FCSTD DOCUMENT  (FreeCAD 0.21R33771 (Git))
Label: Assembly
License: All rights reserved
LicenseURL: http://en.wikipedia.org/wiki/All_rights_reserved
objects: App::Link×43, Part::Feature×8, App::Part×8, PartDesign::CoordinateSystem×7, App::DocumentObjectGroup×3, App::FeaturePython×1
note: 15 computed .brp shape members not serialized (recipe doc carries the construction recipe); baked Part::Feature solids carry a one-line shape summary decoded from their .brp
EXTERNAL_REF file=Azi Plate.FCStd obj=Local_CS
EXTERNAL_REF file=Azi Plate.FCStd obj=Body
EXTERNAL_REF file=Alt Plate Center.FCStd obj=Local_CS002
EXTERNAL_REF file=Alt Plate Center.FCStd obj=Body
EXTERNAL_REF file=Alt Plate.FCStd obj=Local_CS
EXTERNAL_REF file=Alt Plate Center.FCStd obj=Local_CS
EXTERNAL_REF file=Alt Plate.FCStd obj=Body
EXTERNAL_REF file=Alt Plate.FCStd obj=Local_CS001
EXTERNAL_REF file=Alt Plate Center.FCStd obj=Local_CS001
EXTERNAL_REF file=Alt Plate Center.FCStd obj=Local_CS004
EXTERNAL_REF file=Pin.FCStd obj=Local_CS
EXTERNAL_REF file=Pin.FCStd obj=Body
EXTERNAL_REF file=Alt Plate.FCStd obj=Local_CS002
EXTERNAL_REF file=Couple Plate.FCStd obj=Local_CS004
EXTERNAL_REF file=Couple Plate.FCStd obj=Body
EXTERNAL_REF file=Couple Plate.FCStd obj=Local_CS
EXTERNAL_REF file=Disk.FCStd obj=Local_CS
EXTERNAL_REF file=Disk.FCStd obj=Body002
EXTERNAL_REF file=Spacer.FCStd obj=Local_CS001
EXTERNAL_REF file=Spacer.FCStd obj=Body
EXTERNAL_REF file=Spacer.FCStd obj=Local_CS
EXTERNAL_REF file=Lower Bearing Block.FCStd obj=Local_CS
EXTERNAL_REF file=Lower Bearing Block.FCStd obj=Body
EXTERNAL_REF file=Lower Bearing Block.FCStd obj=Local_CS001
EXTERNAL_REF file=Connector Plate.FCStd obj=Local_CS001
EXTERNAL_REF file=Lower Bearing Block.FCStd obj=Local_CS003
EXTERNAL_REF file=Connector Plate.FCStd obj=Body
EXTERNAL_REF file=Connector Plate.FCStd obj=Local_CS
EXTERNAL_REF file=Upper Bearing Block.FCStd obj=Local_CS
EXTERNAL_REF file=Upper Bearing Block.FCStd obj=Body
EXTERNAL_REF file=Hand Nut.FCStd obj=Local_CS
EXTERNAL_REF file=Hand Nut.FCStd obj=Body
EXTERNAL_REF file=Upper Bearing Block.FCStd obj=Local_CS001
EXTERNAL_REF file=Upper Plate.FCStd obj=Local_CS
EXTERNAL_REF file=Upper Plate.FCStd obj=Body004
EXTERNAL_REF file=Upper Plate.FCStd obj=Local_CS005
EXTERNAL_REF file=Flange Bearing.FCStd obj=Local_CS
EXTERNAL_REF file=Upper Plate.FCStd obj=Local_CS003
EXTERNAL_REF file=Flange Bearing.FCStd obj=Body003
EXTERNAL_REF file=Upper Plate.FCStd obj=Local_CS004
EXTERNAL_REF file=Upper Plate.FCStd obj=Local_CS001
EXTERNAL_REF file=Upper Plate.FCStd obj=Local_CS002
EXTERNAL_REF file=Motor Plate.FCStd obj=Local_CS
EXTERNAL_REF file=Upper Plate.FCStd obj=Local_CS007
EXTERNAL_REF file=Motor Plate.FCStd obj=Body
EXTERNAL_REF file=Upper Plate.FCStd obj=Local_CS006
EXTERNAL_REF file=Flange Bearing.FCStd obj=Local_CS001
EXTERNAL_REF file=Motor Plate.FCStd obj=Local_CS001
EXTERNAL_REF file=Holder.FCStd obj=Local_CS
EXTERNAL_REF file=Holder.FCStd obj=Body
EXTERNAL_REF file=Holder.FCStd obj=Local_CS001
EXTERNAL_REF file=Holder Pad.FCStd obj=Local_CS
EXTERNAL_REF file=Holder Pad.FCStd obj=Body
EXTERNAL_REF file=Channel.FCStd obj=DatumPoint
EXTERNAL_REF file=Holder Pad.FCStd obj=Local_CS001
EXTERNAL_REF file=Channel.FCStd obj=Body
EXTERNAL_REF file=Anchor Plate.FCStd obj=Body
EXTERNAL_REF file=Anchor Plate.FCStd obj=Local_CS001
EXTERNAL_REF file=Anchor Plate.FCStd obj=Local_CS002
EXTERNAL_REF file=Alt Plate Center.FCStd obj=Local_CS003

FEATURE [PartDesign::CoordinateSystem] LCS_Origin
  AttacherType = Attacher::AttachEngine3D
  MapMode = 2
  Support = -> [X_Axis]
FEATURE [App::DocumentObjectGroup] Constraints
FEATURE [App::FeaturePython] Variables  # WARN: FeaturePython — macro-defined, semantics opaque (R4)
  Type = App::PropertyContainer
  alt = -90
  azi = -10
  dec = 0
  ra = 180
FEATURE [App::DocumentObjectGroup] Configurations
FEATURE [App::Link] Azi_Plate  label="Azi Plate"
  AttachedBy = #Local_CS
  AttachedTo = Alt_Plate_Center#Local_CS001
  AttachmentOffset = pos=(0,0,0) rot=(1,0,0;3.14159rad)
  LinkPlacement = pos=(5e-16,3e-16,-6.35) rot=(0,0,-1;1.5708rad)
  LinkedObject = -> <external Azi Plate.FCStd>#Body
  Placement = pos=(5e-16,3e-16,-6.35) rot=(0,0,-1;1.5708rad)
  SolverId = Asm4EE
  expr: Placement = LCS_Origin.Placement * AttachmentOffset * Azi_Plate#Local_CS.Placement ^ -1
FEATURE [App::Link] Alt_Plate_Center  label="Alt Plate Center"
  AttachedBy = #Local_CS002
  AttachedTo = Azi_Plate#Local_CS
  LinkPlacement = pos=(2.5e-15,6.5e-15,16) rot=(0,0,1;0rad)
  LinkedObject = -> <external Alt Plate Center.FCStd>#Body
  Placement = pos=(2.5e-15,6.5e-15,16) rot=(0,0,1;0rad)
  SolverId = Asm4EE
  expr: Placement = Azi_Plate.Placement * Azi_Plate#Local_CS.Placement * AttachmentOffset * Alt_Plate_Center#Local_CS002.Placement ^ -1
FEATURE [App::Link] Alt_Plate  label="Alt Plate"
  AttachedBy = #Local_CS001
  AttachedTo = Alt_Plate_Center#Local_CS001
  AttachmentOffset = pos=(0,0,1.6) rot=(0,0,1;-1.5708rad)
  LinkPlacement = pos=(4e-15,-17.475,32.0697) rot=(0,-1,0;4.71239rad)
  LinkedObject = -> <external Alt Plate.FCStd>#Body
  Placement = pos=(4e-15,-17.475,32.0697) rot=(0,-1,0;4.71239rad)
  SolverId = Asm4EE
  expr: .AttachmentOffset.Rotation.Angle = Variables.alt
  expr: Placement = Alt_Plate_Center.Placement * Alt_Plate_Center#Local_CS.Placement * AttachmentOffset * Alt_Plate#Local_CS.Placement ^ -1
FEATURE [App::Link] Alt_Plate001  label="Alt Plate001"
  AttachedBy = #Local_CS001
  AttachedTo = Alt_Plate_Center#Local_CS
  AttachmentOffset = pos=(0,0,-1.6) rot=(0,0,1;-1.5708rad)
  LinkPlacement = pos=(4.9e-15,17.475,32.0697) rot=(0,-1,0;4.71239rad)
  LinkedObject = -> <external Alt Plate.FCStd>#Body
  Placement = pos=(4.9e-15,17.475,32.0697) rot=(0,-1,0;4.71239rad)
  SolverId = Asm4EE
  expr: .AttachmentOffset.Rotation.Angle = Variables.alt
  expr: Placement = Alt_Plate_Center.Placement * Alt_Plate_Center#Local_CS001.Placement * AttachmentOffset * Alt_Plate#Local_CS001.Placement ^ -1
FEATURE [App::Link] Pin
  AttachedBy = #Local_CS
  AttachedTo = Alt_Plate_Center#Local_CS004
  AttachmentOffset = pos=(0,0,0) rot=(0.707107,0.707107,0;3.14159rad)
  LinkPlacement = pos=(-0.000223577,-8.77746e-06,16) rot=(0,1,-2e-06;3.14159rad)
  LinkedObject = -> <external Pin.FCStd>#Body
  Placement = pos=(-0.000223577,-8.77746e-06,16) rot=(0,1,-2e-06;3.14159rad)
  SolverId = Asm4EE
  expr: Placement = Alt_Plate_Center.Placement * Alt_Plate_Center#Local_CS004.Placement * AttachmentOffset * Pin#Local_CS.Placement ^ -1
FEATURE [App::Link] Couple_Plate  label="Couple Plate"
  AttachedBy = #Local_CS004
  AttachedTo = Alt_Plate#Local_CS002
  AttachmentOffset = pos=(0,0,0) rot=(0.707107,-0.707107,0;3.14159rad)
  LinkPlacement = pos=(50,-3.18,32.0697) rot=(-0.57735,0.57735,0.57735;4.18879rad)
  LinkedObject = -> <external Couple Plate.FCStd>#Body
  Placement = pos=(50,-3.18,32.0697) rot=(-0.57735,0.57735,0.57735;4.18879rad)
  SolverId = Asm4EE
  expr: Placement = Alt_Plate.Placement * Alt_Plate#Local_CS002.Placement * AttachmentOffset * Couple_Plate#Local_CS004.Placement ^ -1
FEATURE [App::Link] Disk
  AttachedBy = #Local_CS
  AttachedTo = Couple_Plate#Local_CS
  AttachmentOffset = pos=(0,0,0) rot=(1,0,0;3.14159rad)
  LinkPlacement = pos=(59.525,-3.18,32.0697) rot=(0.57735,-0.57735,-0.57735;2.0944rad)
  LinkedObject = -> <external Disk.FCStd>#Body002
  Placement = pos=(59.525,-3.18,32.0697) rot=(0.57735,-0.57735,-0.57735;2.0944rad)
  SolverId = Asm4EE
  expr: Placement = Couple_Plate.Placement * Couple_Plate#Local_CS.Placement * AttachmentOffset * Disk#Local_CS.Placement ^ -1
FEATURE [App::Link] Spacer
  AttachedBy = #Local_CS001
  AttachedTo = Disk#Local_CS
  AttachmentOffset = pos=(0,0,-10) rot=(1,0,0;3.14159rad)
  LinkPlacement = pos=(60,-3.18,32.0697) rot=(0.57735,0.57735,0.57735;2.0944rad)
  LinkedObject = -> <external Spacer.FCStd>#Body
  Placement = pos=(60,-3.18,32.0697) rot=(0.57735,0.57735,0.57735;2.0944rad)
  SolverId = Asm4EE
  expr: Placement = Disk.Placement * Disk#Local_CS.Placement * AttachmentOffset * Spacer#Local_CS001.Placement ^ -1
FEATURE [PartDesign::CoordinateSystem] LCS_0
  AttacherType = Attacher::AttachEngine3D
  MapMode = 2
  Support = -> [X_Axis001]
FEATURE [Part::Feature] Part__Feature  label="5972K91_Ball Bearing"
  shape: bbox 22 x 22 x 7 mm, 54 faces, 14 solids (baked)
FEATURE [App::Part] Bearing
  Group = -> [LCS_0,Part__Feature]
  Origin = -> Origin001
FEATURE [App::Link] Bearing001
  AttachedBy = #LCS_0
  AttachedTo = Spacer#Local_CS
  AttachmentOffset = pos=(0,0,-3) rot=(0,0,1;0rad)
  LinkPlacement = pos=(74,-3.18,32.0697) rot=(0.707107,0,-0.707107;3.14159rad)
  LinkedObject = -> Bearing
  Placement = pos=(74,-3.18,32.0697) rot=(0.707107,0,-0.707107;3.14159rad)
  SolverId = Asm4EE
  expr: Placement = Spacer.Placement * Spacer#Local_CS.Placement * AttachmentOffset * LCS_0.Placement ^ -1
FEATURE [App::Link] Lower_Bearing_Block  label="Lower Bearing Block"
  AttachedBy = #Local_CS
  AttachedTo = Bearing001#LCS_0
  AttachmentOffset = pos=(0,0,0) rot=(0,0,1;4.71239rad)
  LinkPlacement = pos=(86.375,-3.18,51.1197) rot=(0.707107,-0.707107,0;3.14159rad)
  LinkedObject = -> <external Lower Bearing Block.FCStd>#Body
  Placement = pos=(86.375,-3.18,51.1197) rot=(0.707107,-0.707107,0;3.14159rad)
  SolverId = Asm4EE
  expr: .AttachmentOffset.Rotation.Angle = 90 + Variables.ra
  expr: Placement = Bearing001.Placement * LCS_0.Placement * AttachmentOffset * Lower_Bearing_Block#Local_CS.Placement ^ -1
FEATURE [App::Link] Bearing002
  AttachedBy = #LCS_0
  AttachedTo = Lower_Bearing_Block#Local_CS001
  LinkPlacement = pos=(98.75,-3.18,32.0697) rot=(-0.57735,-0.57735,0.57735;2.0944rad)
  LinkedObject = -> Bearing
  Placement = pos=(98.75,-3.18,32.0697) rot=(-0.57735,-0.57735,0.57735;2.0944rad)
  SolverId = Asm4EE
  expr: Placement = Lower_Bearing_Block.Placement * Lower_Bearing_Block#Local_CS001.Placement * AttachmentOffset * LCS_0.Placement ^ -1
FEATURE [App::Link] Connector_Plate  label="Connector Plate"
  AttachedBy = #Local_CS001
  AttachedTo = Lower_Bearing_Block#Local_CS003
  AttachmentOffset = pos=(19.05,0,0) rot=(0,0,1;0rad)
  LinkPlacement = pos=(86.375,12.695,64.6322) rot=(-0.57735,0.57735,0.57735;2.0944rad)
  LinkedObject = -> <external Connector Plate.FCStd>#Body
  Placement = pos=(86.375,12.695,64.6322) rot=(-0.57735,0.57735,0.57735;2.0944rad)
  SolverId = Asm4EE
  expr: Placement = Lower_Bearing_Block.Placement * Lower_Bearing_Block#Local_CS003.Placement * AttachmentOffset * Connector_Plate#Local_CS001.Placement ^ -1
FEATURE [App::Link] Connector_Plate001  label="Connector Plate001"
  AttachedBy = #Local_CS001
  AttachedTo = Lower_Bearing_Block#Local_CS003
  AttachmentOffset = pos=(-19.05,0,0) rot=(0,0,1;0rad)
  LinkPlacement = pos=(86.375,-25.405,64.6322) rot=(-0.57735,0.57735,0.57735;2.0944rad)
  LinkedObject = -> <external Connector Plate.FCStd>#Body
  Placement = pos=(86.375,-25.405,64.6322) rot=(-0.57735,0.57735,0.57735;2.0944rad)
  SolverId = Asm4EE
  expr: Placement = Lower_Bearing_Block.Placement * Lower_Bearing_Block#Local_CS003.Placement * AttachmentOffset * Connector_Plate#Local_CS001.Placement ^ -1
FEATURE [App::Link] Upper_Bearing_Block  label="Upper Bearing Block"
  AttachedBy = #Local_CS
  AttachedTo = Connector_Plate#Local_CS
  AttachmentOffset = pos=(0,3.5,-19.05) rot=(0.57735,-0.57735,0.57735;2.0944rad)
  LinkPlacement = pos=(86.375,-3.18,97.1947) rot=(0.707107,0.707107,0;3.14159rad)
  LinkedObject = -> <external Upper Bearing Block.FCStd>#Body
  Placement = pos=(86.375,-3.18,97.1947) rot=(0.707107,0.707107,0;3.14159rad)
  SolverId = Asm4EE
  expr: Placement = Connector_Plate.Placement * Connector_Plate#Local_CS.Placement * AttachmentOffset * Upper_Bearing_Block#Local_CS.Placement ^ -1
FEATURE [App::Link] Hand_Nut  label="Hand Nut"
  AttachedBy = #Local_CS
  AttachedTo = Bearing002#LCS_0
  AttachmentOffset = pos=(0,0,-4) rot=(0,0,1;0rad)
  LinkPlacement = pos=(114.25,-3.18,32.0697) rot=(-0.57735,-0.57735,0.57735;2.0944rad)
  LinkedObject = -> <external Hand Nut.FCStd>#Body
  Placement = pos=(114.25,-3.18,32.0697) rot=(-0.57735,-0.57735,0.57735;2.0944rad)
  SolverId = Asm4EE
  expr: Placement = Bearing002.Placement * LCS_0.Placement * AttachmentOffset * Hand_Nut#Local_CS.Placement ^ -1
FEATURE [App::Link] Upper_Plate  label="Upper Plate"
  AttachedBy = #Local_CS
  AttachedTo = Upper_Bearing_Block#Local_CS001
  AttachmentOffset = pos=(0,0,0) rot=(0,0,1;3.14159rad)
  LinkPlacement = pos=(86.375,-3.18,119.42) rot=(0,0,-1;1.5708rad)
  LinkedObject = -> <external Upper Plate.FCStd>#Body004
  Placement = pos=(86.375,-3.18,119.42) rot=(0,0,-1;1.5708rad)
  SolverId = Asm4EE
  expr: Placement = Upper_Bearing_Block.Placement * Upper_Bearing_Block#Local_CS001.Placement * AttachmentOffset * Upper_Plate#Local_CS.Placement ^ -1
FEATURE [App::Link] Bearing003
  AttachedBy = #LCS_0
  AttachedTo = Upper_Plate#Local_CS005
  LinkPlacement = pos=(86.375,-3.18,116.245) rot=(0,0,-1;1.5708rad)
  LinkedObject = -> Bearing
  Placement = pos=(86.375,-3.18,116.245) rot=(0,0,-1;1.5708rad)
  SolverId = Asm4EE
  expr: Placement = Upper_Plate.Placement * Upper_Plate#Local_CS005.Placement * AttachmentOffset * LCS_0.Placement ^ -1
FEATURE [App::Link] Bearing004
  AttachedBy = #LCS_0
  AttachedTo = Upper_Bearing_Block#Local_CS
  AttachmentOffset = pos=(0,0,15) rot=(0,0,1;0rad)
  LinkPlacement = pos=(86.375,-3.18,85.6947) rot=(0.707107,0.707107,0;3.14159rad)
  LinkedObject = -> Bearing
  Placement = pos=(86.375,-3.18,85.6947) rot=(0.707107,0.707107,0;3.14159rad)
  SolverId = Asm4EE
  expr: Placement = Upper_Bearing_Block.Placement * Upper_Bearing_Block#Local_CS.Placement * AttachmentOffset * LCS_0.Placement ^ -1
FEATURE [App::Link] Spacer001
  AttachedBy = #Local_CS
  AttachedTo = Upper_Plate#Local_CS005
  AttachmentOffset = pos=(0,0,3) rot=(0,0,1;0rad)
  LinkPlacement = pos=(86.375,-3.18,130.245) rot=(0,1,0;3.14159rad)
  LinkedObject = -> <external Spacer.FCStd>#Body
  Placement = pos=(86.375,-3.18,130.245) rot=(0,1,0;3.14159rad)
  SolverId = Asm4EE
  expr: Placement = Upper_Plate.Placement * Upper_Plate#Local_CS005.Placement * AttachmentOffset * Spacer#Local_CS.Placement ^ -1
FEATURE [App::Link] Flange_Bearing  label="Flange Bearing"
  AttachedBy = #Local_CS
  AttachedTo = Upper_Plate#Local_CS003
  AttachmentOffset = pos=(0,0,0) rot=(1,0,0;3.14159rad)
  LinkPlacement = pos=(56.375,38.82,95.0697) rot=(1,0,0;3.14159rad)
  LinkedObject = -> <external Flange Bearing.FCStd>#Body003
  Placement = pos=(56.375,38.82,95.0697) rot=(1,0,0;3.14159rad)
  SolverId = Asm4EE
  expr: Placement = Upper_Plate.Placement * Upper_Plate#Local_CS003.Placement * AttachmentOffset * Flange_Bearing#Local_CS.Placement ^ -1
FEATURE [App::Link] Flange_Bearing001  label="Flange Bearing001"
  AttachedBy = #Local_CS
  AttachedTo = Upper_Plate#Local_CS004
  AttachmentOffset = pos=(0,0,0) rot=(1,0,0;3.14159rad)
  LinkPlacement = pos=(56.375,-61.18,95.0697) rot=(1,0,0;3.14159rad)
  LinkedObject = -> <external Flange Bearing.FCStd>#Body003
  Placement = pos=(56.375,-61.18,95.0697) rot=(1,0,0;3.14159rad)
  SolverId = Asm4EE
  expr: Placement = Upper_Plate.Placement * Upper_Plate#Local_CS004.Placement * AttachmentOffset * Flange_Bearing#Local_CS.Placement ^ -1
FEATURE [App::Link] Flange_Bearing002  label="Flange Bearing002"
  AttachedBy = #Local_CS
  AttachedTo = Upper_Plate#Local_CS001
  LinkPlacement = pos=(23.375,-61.18,137.42) rot=(0,0,-1;3.14159rad)
  LinkedObject = -> <external Flange Bearing.FCStd>#Body003
  Placement = pos=(23.375,-61.18,137.42) rot=(0,0,-1;3.14159rad)
  SolverId = Asm4EE
  expr: Placement = Upper_Plate.Placement * Upper_Plate#Local_CS001.Placement * AttachmentOffset * Flange_Bearing#Local_CS.Placement ^ -1
FEATURE [App::Link] Flange_Bearing003  label="Flange Bearing003"
  AttachedBy = #Local_CS
  AttachedTo = Upper_Plate#Local_CS002
  LinkPlacement = pos=(23.375,38.82,137.42) rot=(0,0,-1;3.14159rad)
  LinkedObject = -> <external Flange Bearing.FCStd>#Body003
  Placement = pos=(23.375,38.82,137.42) rot=(0,0,-1;3.14159rad)
  SolverId = Asm4EE
  expr: Placement = Upper_Plate.Placement * Upper_Plate#Local_CS002.Placement * AttachmentOffset * Flange_Bearing#Local_CS.Placement ^ -1
FEATURE [App::Link] Motor_Plate  label="Motor Plate"
  AttachedBy = #Local_CS
  AttachedTo = Upper_Plate#Local_CS007
  LinkPlacement = pos=(156.375,-54.83,86.0697) rot=(0.707107,-0.707107,0;3.14159rad)
  LinkedObject = -> <external Motor Plate.FCStd>#Body
  Placement = pos=(156.375,-54.83,86.0697) rot=(0.707107,-0.707107,0;3.14159rad)
  SolverId = Asm4EE
  expr: Placement = Upper_Plate.Placement * Upper_Plate#Local_CS007.Placement * AttachmentOffset * Motor_Plate#Local_CS.Placement ^ -1
FEATURE [App::Link] Motor_Plate001  label="Motor Plate001"
  AttachedBy = #Local_CS
  AttachedTo = Upper_Plate#Local_CS006
  LinkPlacement = pos=(183.375,54.82,86.0697) rot=(0.707107,-0.707107,0;3.14159rad)
  LinkedObject = -> <external Motor Plate.FCStd>#Body
  Placement = pos=(183.375,54.82,86.0697) rot=(0.707107,-0.707107,0;3.14159rad)
  SolverId = Asm4EE
  expr: Placement = Upper_Plate.Placement * Upper_Plate#Local_CS006.Placement * AttachmentOffset * Motor_Plate#Local_CS.Placement ^ -1
FEATURE [PartDesign::CoordinateSystem] LCS_001
  AttacherType = Attacher::AttachEngine3D
  MapMode = 2
  Support = -> [X_Axis002]
FEATURE [Part::Feature] Part__Feature001  label="Threaded Rod001"
  shape: bbox 10.16 x 10.16 x 151.2 mm, 225 faces (baked)
FEATURE [App::Part] Threaded_Rod  label="Threaded Rod"
  Group = -> [LCS_001,Part__Feature001]
  Origin = -> Origin002
FEATURE [App::Link] Threaded_Rod001  label="Threaded Rod002"
  AttachedBy = #LCS_001
  AttachedTo = Flange_Bearing001#Local_CS001
  AttachmentOffset = pos=(0,0,-48) rot=(0,0,1;0rad)
  LinkPlacement = pos=(56.375,-5.18,95.0697) rot=(0,-0.707107,0.707107;3.14159rad)
  LinkedObject = -> Threaded_Rod
  Placement = pos=(56.375,-5.18,95.0697) rot=(0,-0.707107,0.707107;3.14159rad)
  SolverId = Asm4EE
  expr: Placement = Flange_Bearing001.Placement * Flange_Bearing#Local_CS001.Placement * AttachmentOffset * LCS_001.Placement ^ -1
FEATURE [App::Link] Threaded_Rod002  label="Threaded Rod003"
  AttachedBy = #LCS_001
  AttachedTo = Flange_Bearing002#Local_CS001
  AttachmentOffset = pos=(0,0,-48) rot=(0,0,1;0rad)
  LinkPlacement = pos=(23.375,-5.18,137.42) rot=(1,0,0;1.5708rad)
  LinkedObject = -> Threaded_Rod
  Placement = pos=(23.375,-5.18,137.42) rot=(1,0,0;1.5708rad)
  SolverId = Asm4EE
  expr: Placement = Flange_Bearing002.Placement * Flange_Bearing#Local_CS001.Placement * AttachmentOffset * LCS_001.Placement ^ -1
FEATURE [App::Link] Disk001
  AttachedBy = #Local_CS
  AttachedTo = Spacer001#Local_CS001
  AttachmentOffset = pos=(0,0,0) rot=(0,0,1;3.14159rad)
  LinkPlacement = pos=(86.375,-3.18,139.77) rot=(1,0,0;3.14159rad)
  LinkedObject = -> <external Disk.FCStd>#Body002
  Placement = pos=(86.375,-3.18,139.77) rot=(1,0,0;3.14159rad)
  SolverId = Asm4EE
  expr: .AttachmentOffset.Rotation.Angle = 180 + Variables.dec
  expr: Placement = Spacer001.Placement * Spacer#Local_CS001.Placement * AttachmentOffset * Disk#Local_CS.Placement ^ -1
FEATURE [PartDesign::CoordinateSystem] LCS_002
  AttacherType = Attacher::AttachEngine3D
  MapMode = 2
  Support = -> [X_Axis003]
FEATURE [Part::Feature] Part__Feature002  label="Pulley part01 GT2 6mm"
  Placement = pos=(-6.98828,1.39514,32.2) rot=(0,0,1;0rad)
  shape: bbox 37.7 x 37.7 x 18 mm, 612 faces (baked)
FEATURE [Part::Feature] Part__Feature003  label="Gear 60pitch part02"
  Placement = pos=(-6.98828,1.39514,41.28) rot=(0,0,1;0rad)
  shape: bbox 41.15 x 41.15 x 1.92 mm, 16 faces (baked)
FEATURE [Part::Feature] Part__Feature004  label="Gear 60pitch part003"
  Placement = pos=(-6.98828,1.39514,34.12) rot=(-0.195284,0.980747,0;3.14159rad)
  shape: bbox 41.15 x 41.15 x 1.92 mm, 16 faces (baked)
FEATURE [App::Part] _0pitch_pulley_GT2_6mm_ASSEMBLY  label="60pitch pulley GT2 6mm ASSEMBLY"
  Group = -> [Part__Feature002,Part__Feature003,Part__Feature004]
  Origin = -> Origin004
  Placement = pos=(7,-1,-37.7) rot=(0,0,1;0rad)
FEATURE [App::Part] Pulley
  Group = -> [LCS_002,_0pitch_pulley_GT2_6mm_ASSEMBLY]
  Origin = -> Origin003
FEATURE [App::Link] Pulley001
  AttachedBy = #LCS_002
  AttachedTo = Flange_Bearing001#Local_CS001
  AttachmentOffset = pos=(0,0,20) rot=(0,1,0;3.14159rad)
  LinkPlacement = pos=(56.375,-73.18,95.0697) rot=(-1,0,0;1.5708rad)
  LinkedObject = -> Pulley
  Placement = pos=(56.375,-73.18,95.0697) rot=(-1,0,0;1.5708rad)
  SolverId = Asm4EE
  expr: Placement = Flange_Bearing001.Placement * Flange_Bearing#Local_CS001.Placement * AttachmentOffset * LCS_002.Placement ^ -1
FEATURE [App::Link] Pulley002
  AttachedBy = #LCS_002
  AttachedTo = Flange_Bearing003#Local_CS001
  AttachmentOffset = pos=(0,0,-20) rot=(0,0,1;0rad)
  LinkPlacement = pos=(23.375,66.82,137.42) rot=(1,0,0;1.5708rad)
  LinkedObject = -> Pulley
  Placement = pos=(23.375,66.82,137.42) rot=(1,0,0;1.5708rad)
  SolverId = Asm4EE
  expr: Placement = Flange_Bearing003.Placement * Flange_Bearing#Local_CS001.Placement * AttachmentOffset * LCS_002.Placement ^ -1
FEATURE [PartDesign::CoordinateSystem] LCS_003
  AttacherType = Attacher::AttachEngine3D
  MapMode = 2
  Support = -> [X_Axis005]
FEATURE [Part::Feature] Part__Feature005  label="Cut"
  shape: bbox 45.91 x 45.91 x 58.29 mm, 373 faces, 15 solids (baked)
FEATURE [App::Part] Motor
  Group = -> [LCS_003,Part__Feature005]
  Origin = -> Origin005
FEATURE [App::Link] Motor001
  AttachedBy = #LCS_003
  AttachedTo = Motor_Plate001#Local_CS001
  AttachmentOffset = pos=(0,0,3) rot=(1,0,0;3.14159rad)
  LinkPlacement = pos=(183.375,48.645,86.0697) rot=(0,0.707107,0.707107;3.14159rad)
  LinkedObject = -> Motor
  Placement = pos=(183.375,48.645,86.0697) rot=(0,0.707107,0.707107;3.14159rad)
  SolverId = Asm4EE
  expr: Placement = Motor_Plate001.Placement * Motor_Plate#Local_CS001.Placement * AttachmentOffset * LCS_003.Placement ^ -1
FEATURE [App::Link] Motor002
  AttachedBy = #LCS_003
  AttachedTo = Motor_Plate#Local_CS001
  AttachmentOffset = pos=(0,0,-3) rot=(0,0,1;0rad)
  LinkPlacement = pos=(156.375,-55.005,86.0697) rot=(0,-0.707107,0.707107;3.14159rad)
  LinkedObject = -> Motor
  Placement = pos=(156.375,-55.005,86.0697) rot=(0,-0.707107,0.707107;3.14159rad)
  SolverId = Asm4EE
  expr: Placement = Motor_Plate.Placement * Motor_Plate#Local_CS001.Placement * AttachmentOffset * LCS_003.Placement ^ -1
FEATURE [App::Link] Holder
  AttachedBy = #Local_CS
  AttachedTo = Disk001#Local_CS
  AttachmentOffset = pos=(0,0,-10) rot=(0,0,1;0rad)
  LinkPlacement = pos=(86.375,-3.18,140.245) rot=(0,0,-1;3.14159rad)
  LinkedObject = -> <external Holder.FCStd>#Body
  Placement = pos=(86.375,-3.18,140.245) rot=(0,0,-1;3.14159rad)
  SolverId = Asm4EE
  expr: Placement = Disk001.Placement * Disk#Local_CS.Placement * AttachmentOffset * Holder#Local_CS.Placement ^ -1
FEATURE [App::Link] Hand_Nut001  label="Hand Nut001"
  AttachedBy = #Local_CS
  AttachedTo = Upper_Bearing_Block#Local_CS
  AttachmentOffset = pos=(0,0,19) rot=(0,-1,0;3.14159rad)
  LinkPlacement = pos=(86.375,-3.18,70.1947) rot=(0,0,-1;1.5708rad)
  LinkedObject = -> <external Hand Nut.FCStd>#Body
  Placement = pos=(86.375,-3.18,70.1947) rot=(0,0,-1;1.5708rad)
  SolverId = Asm4EE
  expr: Placement = Upper_Bearing_Block.Placement * Upper_Bearing_Block#Local_CS.Placement * AttachmentOffset * Hand_Nut#Local_CS.Placement ^ -1
FEATURE [App::Link] Holder_Pad  label="Holder Pad"
  AttachedBy = #Local_CS
  AttachedTo = Holder#Local_CS001
  LinkPlacement = pos=(86.375,-3.18,160.745) rot=(0,0,-1;1.5708rad)
  LinkedObject = -> <external Holder Pad.FCStd>#Body
  Placement = pos=(86.375,-3.18,160.745) rot=(0,0,-1;1.5708rad)
  SolverId = Asm4EE
  expr: Placement = Holder.Placement * Holder#Local_CS001.Placement * AttachmentOffset * Holder_Pad#Local_CS.Placement ^ -1
FEATURE [App::Link] Channel
  AttachedBy = #DatumPoint
  AttachedTo = Holder_Pad#Local_CS001
  LinkPlacement = pos=(296.127,-3.18,161.945) rot=(0,0,-1;1.5708rad)
  LinkedObject = -> <external Channel.FCStd>#Body
  Placement = pos=(296.127,-3.18,161.945) rot=(0,0,-1;1.5708rad)
  SolverId = Asm4EE
  expr: Placement = Holder_Pad.Placement * Holder_Pad#Local_CS001.Placement * AttachmentOffset * Channel#DatumPoint.Placement ^ -1
FEATURE [App::Link] Anchor_Plate  label="Anchor Plate"
  AttachedBy = #Local_CS
  AttachedTo = Azi_Plate#Local_CS
  AttachmentOffset = pos=(0,0,6.35) rot=(0.707107,0.707107,0;3.14159rad)
  LinkPlacement = pos=(-3e-16,-1.9e-15,-12.7) rot=(0,0,1;4.53786rad)
  LinkedObject = -> <external Anchor Plate.FCStd>#Body
  Placement = pos=(-3e-16,-1.9e-15,-12.7) rot=(0,0,1;4.53786rad)
  SolverId = Asm4EE
  expr: .Placement.Rotation.Angle = 270 + Variables.azi
FEATURE [PartDesign::CoordinateSystem] LCS_004
  AttacherType = Attacher::AttachEngine3D
  MapMode = 2
  Support = -> [X_Axis006]
FEATURE [App::Link] Anchor_Rod  label="Anchor Rod001"
  AttachedBy = #LCS_004
  AttachedTo = Anchor_Plate#Local_CS001
  LinkPlacement = pos=(6.07769,34.4683,-12.7) rot=(-0.996195,0.087156,0;3.14159rad)
  LinkedObject = -> Anchor_ROd
  Placement = pos=(6.07769,34.4683,-12.7) rot=(-0.996195,0.087156,0;3.14159rad)
  SolverId = Asm4EE
  expr: Placement = Anchor_Plate.Placement * Anchor_Plate#Local_CS001.Placement * AttachmentOffset * LCS_004.Placement ^ -1
FEATURE [App::Link] Anchor_Rod_002  label="Anchor Rod_002"
  AttachedBy = #LCS_004
  AttachedTo = Anchor_Plate#Local_CS002
  LinkPlacement = pos=(-6.07769,-34.4683,-12.7) rot=(-0.996195,0.087156,0;3.14159rad)
  LinkedObject = -> Anchor_ROd
  Placement = pos=(-6.07769,-34.4683,-12.7) rot=(-0.996195,0.087156,0;3.14159rad)
  SolverId = Asm4EE
  expr: Placement = Anchor_Plate.Placement * Anchor_Plate#Local_CS002.Placement * AttachmentOffset * LCS_004.Placement ^ -1
FEATURE [Part::Feature] Part__Feature007  label="1078N146_Class 10.9 High-Strength Steel Threaded Rod"
  shape: bbox 8.135 x 8.135 x 31.02 mm, 62 faces (baked)
FEATURE [App::Part] Anchor_ROd  label="Anchor Rod"
  Group = -> [LCS_004,Part__Feature007]
  Origin = -> Origin006
FEATURE [PartDesign::CoordinateSystem] LCS_005
  AttacherType = Attacher::AttachEngine3D
  MapMode = 2
  Support = -> [X_Axis007]
FEATURE [Part::Feature] Part__Feature008  label="1078N152_Class 10.9 High-Strength Steel Threaded Rod"
  shape: bbox 8.135 x 8.135 x 80.55 mm, 154 faces (baked)
FEATURE [App::Part] Shaft
  Group = -> [LCS_005,Part__Feature008]
  Origin = -> Origin007
FEATURE [App::DocumentObjectGroup] Parts
  Group = -> [Bearing,Threaded_Rod,Pulley,Motor,Anchor_ROd,Shaft]
FEATURE [App::Link] Shaft001
  AttachedBy = #LCS_005
  AttachedTo = Alt_Plate_Center#Local_CS003
  AttachmentOffset = pos=(0,0,-10) rot=(0,1,0;3.14159rad)
  LinkPlacement = pos=(-40.1511,1.35e-14,16) rot=(-0.707107,0,0.707107;3.14159rad)
  LinkedObject = -> Shaft
  Placement = pos=(-40.1511,1.35e-14,16) rot=(-0.707107,0,0.707107;3.14159rad)
  SolverId = Asm4EE
  expr: Placement = Alt_Plate_Center.Placement * Alt_Plate_Center#Local_CS003.Placement * AttachmentOffset * LCS_005.Placement ^ -1
FEATURE [App::Link] Shaft_1
  AttachedBy = #LCS_005
  AttachedTo = Disk#Local_CS
  LinkPlacement = pos=(50,-3.18,32.0697) rot=(0,-1,0;1.5708rad)
  LinkedObject = -> Shaft
  Placement = pos=(50,-3.18,32.0697) rot=(0,-1,0;1.5708rad)
  SolverId = Asm4EE
  expr: Placement = Disk.Placement * Disk#Local_CS.Placement * AttachmentOffset * LCS_005.Placement ^ -1
FEATURE [App::Link] Shaft_2
  AttachedBy = #LCS_005
  AttachedTo = Holder#Local_CS
  AttachmentOffset = pos=(0,0,0) rot=(1,0,0;3.14159rad)
  LinkPlacement = pos=(86.375,-3.18,140.245) rot=(0,0,1;4.71239rad)
  LinkedObject = -> Shaft
  Placement = pos=(86.375,-3.18,140.245) rot=(0,0,1;4.71239rad)
  SolverId = Asm4EE
  expr: Placement = Holder.Placement * Holder#Local_CS.Placement * AttachmentOffset * LCS_005.Placement ^ -1
FEATURE [App::Link] Shaft002
  AttachedBy = #LCS_005
  AttachedTo = Alt_Plate_Center#Local_CS
  AttachmentOffset = pos=(0,0,26) rot=(0,0,1;0rad)
  LinkPlacement = pos=(4.4e-15,-35.525,32.0697) rot=(0.57735,-0.57735,0.57735;2.0944rad)
  LinkedObject = -> Shaft
  Placement = pos=(4.4e-15,-35.525,32.0697) rot=(0.57735,-0.57735,0.57735;2.0944rad)
  SolverId = Asm4EE
  expr: Placement = Alt_Plate_Center.Placement * Alt_Plate_Center#Local_CS.Placement * AttachmentOffset * LCS_005.Placement ^ -1
FEATURE [App::Part] Assembly
  AssemblyType = Part::Link
  Group = -> [LCS_Origin,Constraints,Variables,Configurations,Azi_Plate,Alt_Plate_Center,Alt_Plate,Alt_Plate001,Pin,Couple_Plate,Disk,Spacer,Bearing001,Lower_Bearing_Block,Bearing002,Connector_Plate,Connector_Plate001,Upper_Bearing_Block,Hand_Nut,Upper_Plate,Bearing003,Bearing004,Spacer001,Flange_Bearing,Flange_Bearing001,Flange_Bearing002,Flange_Bearing003,Motor_Plate,Motor_Plate001,Threaded_Rod001,+17 more]
  Origin = -> Origin
  Type = Assembly

RESOLVED EXTERNAL PARTS (link-assembly join: the EXTERNAL_REF files above that resolve inside this repo's crawl, each included once):
---- part Channel.FCStd = doc fcstd_355a5e1f0a80 ----
FCSTD DOCUMENT  (FreeCAD 0.20R29603 (Git))
Label: Channel
License: All rights reserved
LicenseURL: https://en.wikipedia.org/wiki/All_rights_reserved
objects: TechDraw::DrawViewDimension×7, Sketcher::SketchObject×3, TechDraw::DrawViewPart×3, PartDesign::Pocket×2, PartDesign::Pad×1, PartDesign::Hole×1, PartDesign::Point×1, PartDesign::Body×1, TechDraw::DrawSVGTemplate×1, TechDraw::DrawPage×1
note: 13 computed .brp shape members not serialized (recipe doc carries the construction recipe); baked Part::Feature solids carry a one-line shape summary decoded from their .brp

FEATURE [Sketcher::SketchObject] Sketch
  FullyConstrained = true
  MapMode = 5
  Placement = pos=(0,0,0) rot=(1,0,0;1.5708rad)
  Support = -> [XZ_Plane]
  sketch-geometry (9):
    g0: LineSegment StartX=-12.7 StartY=12.7 StartZ=0 EndX=-12.7 EndY=0 EndZ=0
    g1: LineSegment StartX=-12.7 StartY=0 StartZ=0 EndX=12.7 EndY=0 EndZ=0
    g2: LineSegment StartX=12.7 StartY=0 StartZ=0 EndX=12.7 EndY=12.7 EndZ=0
    g3: LineSegment StartX=12.7 StartY=12.7 StartZ=0 EndX=9.525 EndY=12.7 EndZ=0
    g4: LineSegment StartX=9.525 StartY=12.7 StartZ=0 EndX=9.525 EndY=3.175 EndZ=0
    g5: LineSegment StartX=9.525 StartY=3.175 StartZ=0 EndX=-9.525 EndY=3.175 EndZ=0
    g6: LineSegment StartX=-9.525 StartY=3.175 StartZ=0 EndX=-9.525 EndY=12.7 EndZ=0
    g7: LineSegment StartX=-9.525 StartY=12.7 StartZ=0 EndX=-12.7 EndY=12.7 EndZ=0
    g8: LineSegment StartX=-9.525 StartY=3.175 StartZ=0 EndX=-9.525 EndY=0 EndZ=0
  constraints (26):
    c: Coincident(g0,g1)
    c: Horizontal(g1)
    c: Coincident(g1,g2)
    c: Vertical(g2)
    c: Coincident(g2,g3)
    c: Coincident(g3,g4)
    c: Coincident(g4,g5)
    c: Coincident(g5,g6)
    c: Coincident(g6,g7)
    c: Coincident(g7,g0)
    c: Vertical(g0)
    c: Vertical(g6)
    c: Vertical(g4)
    c: Horizontal(g3)
    c: Horizontal(g7)
    c: Equal(g7,g3)
    c: Equal(g6,g4)
    c: Coincident(g8,g5)
    c: PointOnObject(g8,g1)
    c: Vertical(g8)
    c: Equal(g7,g8)
    c: DistanceX(g3,g3) = 3.175
    c: DistanceX(g1,g1) = 25.4
    c: DistanceY(g2,g2) = 12.7  'height'
    c: Symmetric(g4,g5,g-2)
    c: PointOnObject(g-1,g1)
FEATURE [PartDesign::Pad] Pad
  AlongSketchNormal = false
  Direction = (0,-1,-2e-16)
  Length = 735
  Length2 = 10
  Midplane = true
  Profile = -> Sketch
  ReferenceAxis = -> Sketch [N_Axis]
  Type = 0
FEATURE [Sketcher::SketchObject] Sketch001
  FullyConstrained = false
  MapMode = 5
  Placement = pos=(0,-367.5,0) rot=(1,0,0;1.5708rad)
  Support = -> [Pad]
  expr: Constraints[20] = Sketch.Constraints.height - 5mm
  sketch-geometry (9):
    g0: LineSegment StartX=-33.5342 StartY=9.2875 StartZ=0 EndX=-11.1125 EndY=9.2875 EndZ=0
    g1: LineSegment StartX=-11.1125 StartY=9.2875 StartZ=0 EndX=-11.1125 EndY=6.1125 EndZ=0
    g2: LineSegment StartX=-11.1125 StartY=6.1125 StartZ=0 EndX=-33.5342 EndY=6.1125 EndZ=0
    g3: LineSegment StartX=-33.5342 StartY=6.1125 StartZ=0 EndX=-33.5342 EndY=9.2875 EndZ=0
    g4: LineSegment StartX=33.5342 StartY=6.1125 StartZ=0 EndX=11.1125 EndY=6.1125 EndZ=0
    g5: LineSegment StartX=11.1125 StartY=6.1125 StartZ=0 EndX=11.1125 EndY=9.2875 EndZ=0
    g6: LineSegment StartX=11.1125 StartY=9.2875 StartZ=0 EndX=33.5342 EndY=9.2875 EndZ=0
    g7: LineSegment StartX=33.5342 StartY=9.2875 StartZ=0 EndX=33.5342 EndY=6.1125 EndZ=0
    g8: GeomPoint X=1e-16 Y=7.7 Z=0
  constraints (23):
    c: Coincident(g0,g1)
    c: Coincident(g1,g2)
    c: Coincident(g2,g3)
    c: Coincident(g3,g0)
    c: Horizontal(g0)
    c: Horizontal(g2)
    c: Vertical(g1)
    c: Vertical(g3)
    c: Coincident(g4,g5)
    c: Coincident(g5,g6)
    c: Coincident(g6,g7)
    c: Coincident(g7,g4)
    c: Horizontal(g4)
    c: Horizontal(g6)
    c: Vertical(g7)
    c: PointOnObject(g8,g-2)
    c: Symmetric(g1,g5,g8)
    c: Symmetric(g4,g0,g8)
    c: Horizontal(g4,g1)
    c: Equal(g0,g6)
    c: DistanceY(g-1,g8) = 7.7
    c: DistanceY(g5,g5) = 3.175
    c: DistanceX(g-1,g4) = 11.1125
FEATURE [PartDesign::Pocket] Pocket
  AlongSketchNormal = false
  BaseFeature = -> Pad
  Direction = (0,1,-2e-16)
  Length = 300
  Length2 = 10
  Profile = -> Sketch001
  ReferenceAxis = -> Sketch001 [N_Axis]
  Type = 0
FEATURE [Sketcher::SketchObject] Sketch002
  ExternalGeometry = -> [Pocket]
  FullyConstrained = true
  MapMode = 5
  Placement = pos=(0,0,7e-16) rot=(1,0,0;3.14159rad)
  Support = -> [Pocket]
  sketch-geometry (9):
    g0: Circle CenterX=0 CenterY=352.5 CenterZ=0 NormalX=0 NormalY=0 NormalZ=1 AngleXU=0 Radius=1.6
    g1: Circle CenterX=0 CenterY=262.5 CenterZ=0 NormalX=0 NormalY=0 NormalZ=1 AngleXU=0 Radius=1.6
    g2: ArcOfCircle CenterX=0 CenterY=-252.5 CenterZ=0 NormalX=0 NormalY=0 NormalZ=1 AngleXU=0 Radius=3.175 StartAngle=-2.7e-15 EndAngle=3.14159
    g3: ArcOfCircle CenterX=0 CenterY=-352.5 CenterZ=0 NormalX=0 NormalY=0 NormalZ=1 AngleXU=0 Radius=3.175 StartAngle=3.14159 EndAngle=6.28319
    g4: LineSegment StartX=-3.175 StartY=-252.5 StartZ=0 EndX=-3.175 EndY=-352.5 EndZ=0
    g5: LineSegment StartX=3.175 StartY=-352.5 StartZ=0 EndX=3.175 EndY=-252.5 EndZ=0
    g6: GeomPoint X=0 Y=307.5 Z=0
    g7: GeomPoint X=0 Y=-302.5 Z=0
    g8: Circle CenterX=0 CenterY=307.5 CenterZ=0 NormalX=0 NormalY=0 NormalZ=1 AngleXU=0 Radius=1.6
  constraints (20):
    c: PointOnObject(g1,g-2)
    c: PointOnObject(g0,g-2)
    c: Equal(g1,g0)
    c: Tangent(g2,g4) = -1.5708
    c: Tangent(g4,g3) = -1.5708
    c: Tangent(g3,g5) = -1.5708
    c: Tangent(g5,g2) = -1.5708
    c: PointOnObject(g2,g-2)
    c: PointOnObject(g3,g-2)
    c: DistanceY(g1,g0) = 90
    c: DistanceY(g3,g2) = 100
    c: Radius(g2) = 3.175
    c: Symmetric(g0,g1,g6)
    c: Symmetric(g2,g3,g7)
    c: DistanceY(g7,g6) = 610
    c: Vertical(g4)
    c: Diameter(g0) = 3.2
    c: Coincident(g8,g6)
    c: Equal(g1,g8)
    c: DistanceY(g0,g-3) = 15
FEATURE [PartDesign::Pocket] Pocket001
  AlongSketchNormal = false
  BaseFeature = -> Pocket
  Direction = (0,-2e-16,1)
  Length = 0
  Length2 = 10
  Profile = -> Sketch002 [Edge6,Edge5,Edge4,Edge3]
  ReferenceAxis = -> Sketch002 [N_Axis]
  Type = 3
  UpToFace = -> Pocket [Face12]
FEATURE [PartDesign::Hole] Hole
  BaseFeature = -> Pocket001
  CustomThreadClearance = 0
  Depth = 1485.81
  DepthType = 1
  Diameter = 3.4
  DrillForDepth = false
  DrillPoint = 1
  DrillPointAngle = 118
  HoleCutCountersinkAngle = 90
  HoleCutCustomValues = false
  HoleCutDepth = 0
  HoleCutDiameter = 6.1
  HoleCutType = 2
  ModelThread = false
  Profile = -> Sketch002 [Edge2,Edge1,Edge7]
  Tapered = false
  TaperedAngle = 90
  ThreadClass = 0
  ThreadDepth = 1485.81
  ThreadDepthType = 0
  ThreadDirection = 0
  ThreadFit = 0
  ThreadSize = 9
  ThreadType = 1
  Threaded = false
  UseCustomThreadClearance = false
FEATURE [PartDesign::Point] DatumPoint
  AttacherType = Attacher::AttachEnginePoint
  AttachmentOffset = pos=(0,-200,0) rot=(0,0,1;0rad)
  MapMode = 37
  Placement = pos=(0,-209.752,-1.4e-15) rot=(0,0,1;0rad)
  Support = -> [Hole]
FEATURE [PartDesign::Body] Body  label="Channel"
  Group = -> [Sketch,Sketch001,Sketch002,Pad,Pocket,Pocket001,Hole,DatumPoint]
  Origin = -> Origin
  Tip = -> Hole
FEATURE [TechDraw::DrawSVGTemplate] Template
  Height = 297
  Orientation = 1
  Width = 420
FEATURE [TechDraw::DrawViewPart] View001  label="Top"
  CoarseView = false
  Direction = (0,0,1)
  Focus = 100
  HardHidden = false
  IsoCount = 0
  IsoHidden = false
  IsoVisible = false
  LockPosition = false
  Perspective = false
  Rotation = 0
  Scale = 0.5
  ScaleType = 0
  SeamHidden = false
  SeamVisible = true
  SmoothHidden = false
  SmoothVisible = true
  Source = -> [Hole]
  X = 209.57
  XDirection = (0,-1,0)
  Y = 244.118
FEATURE [TechDraw::DrawViewDimension] Dimension001
  AngleOverride = false
  Arbitrary = false
  ArbitraryTolerances = false
  EqualTolerance = true
  ExtensionAngle = 0
  FormatSpec = %.2w
  FormatSpecOverTolerance = %+.2w
  FormatSpecUnderTolerance = %+.2w
  Inverted = false
  LineAngle = 0
  LockPosition = false
  MeasureType = 1
  OverTolerance = 0
  References2D = -> [View001]
  Rotation = 0
  Scale = 0.5
  ScaleType = 0
  TheoreticalExact = false
  Type = 1
  UnderTolerance = 0
  X = -164.371
  Y = -33.0505
FEATURE [TechDraw::DrawViewDimension] Dimension
  AngleOverride = false
  Arbitrary = false
  ArbitraryTolerances = false
  EqualTolerance = true
  ExtensionAngle = 0
  FormatSpec = %.2w
  FormatSpecOverTolerance = %+.2w
  FormatSpecUnderTolerance = %+.2w
  Inverted = false
  LineAngle = 0
  LockPosition = false
  MeasureType = 1
  OverTolerance = 0
  References2D = -> [View001]
  Rotation = 0
  Scale = 0.5
  ScaleType = 0
  TheoreticalExact = false
  Type = 1
  UnderTolerance = 0
  X = 0.406176
  Y = -32.9406
FEATURE [TechDraw::DrawViewPart] View002  label="Bottom"
  CoarseView = false
  Direction = (0,0,-1)
  Focus = 100
  HardHidden = false
  IsoCount = 0
  IsoHidden = false
  IsoVisible = false
  LockPosition = false
  Perspective = false
  Rotation = 0
  Scale = 0.5
  ScaleType = 0
  SeamHidden = false
  SeamVisible = true
  SmoothHidden = false
  SmoothVisible = true
  Source = -> [Hole]
  X = 209.719
  XDirection = (0,-1,0)
  Y = 176.627
FEATURE [TechDraw::DrawViewDimension] Dimension004
  AngleOverride = false
  Arbitrary = false
  ArbitraryTolerances = false
  EqualTolerance = true
  ExtensionAngle = 0
  FormatSpec = 3X ⌀%.2w THRU ⌵6.1x90°
  FormatSpecOverTolerance = %+.2w
  FormatSpecUnderTolerance = %+.2w
  Inverted = false
  LineAngle = 0
  LockPosition = false
  MeasureType = 1
  OverTolerance = 0
  References2D = -> [View002]
  Rotation = 0
  Scale = 0.5
  ScaleType = 0
  TheoreticalExact = false
  Type = 5
  UnderTolerance = 0
  X = 73.7573
  Y = -30.0116
FEATURE [TechDraw::DrawViewDimension] Dimension005
  AngleOverride = false
  Arbitrary = false
  ArbitraryTolerances = false
  EqualTolerance = true
  ExtensionAngle = 0
  FormatSpec = %.2w (1/4")
  FormatSpecOverTolerance = %+.2w
  FormatSpecUnderTolerance = %+.2w
  Inverted = false
  LineAngle = 0
  LockPosition = false
  MeasureType = 1
  OverTolerance = 0
  References2D = -> [View002]
  Rotation = 0
  Scale = 0.5
  ScaleType = 0
  TheoreticalExact = false
  Type = 2
  UnderTolerance = 0
  X = -99.1893
  Y = -39.547
FEATURE [TechDraw::DrawViewDimension] Dimension006
  AngleOverride = false
  Arbitrary = false
  ArbitraryTolerances = false
  EqualTolerance = true
  ExtensionAngle = 0
  FormatSpec = %.2w
  FormatSpecOverTolerance = %+.2w
  FormatSpecUnderTolerance = %+.2w
  Inverted = false
  LineAngle = 0
  LockPosition = false
  MeasureType = 1
  OverTolerance = 0
  References2D = -> [View001]
  Rotation = 0
  Scale = 0.5
  ScaleType = 0
  TheoreticalExact = false
  Type = 1
  UnderTolerance = 0
  X = 164.448
  Y = -33.1003
FEATURE [TechDraw::DrawViewPart] View  label="Front"
  Caption = 1:1
  CoarseView = false
  Direction = (0,-1,0)
  Focus = 100
  HardHidden = false
  IsoCount = 0
  IsoHidden = false
  IsoVisible = false
  LockPosition = false
  Perspective = false
  Rotation = 0
  ScaleType = 2
  SeamHidden = false
  SeamVisible = true
  SmoothHidden = false
  SmoothVisible = true
  Source = -> [Hole]
  X = 211.419
  XDirection = (1,0,0)
  Y = 112.899
FEATURE [TechDraw::DrawViewDimension] Dimension008
  AngleOverride = false
  Arbitrary = false
  ArbitraryTolerances = false
  EqualTolerance = true
  ExtensionAngle = 0
  FormatSpec = %.2w (1/16")
  FormatSpecOverTolerance = %+.2w
  FormatSpecUnderTolerance = %+.2w
  Inverted = false
  LineAngle = 0
  LockPosition = false
  MeasureType = 1
  OverTolerance = 0
  References2D = -> [View]
  Rotation = 0
  Scale = 0.5
  ScaleType = 0
  TheoreticalExact = false
  Type = 1
  UnderTolerance = 0
  X = -63.1056
  Y = -24.338
FEATURE [TechDraw::DrawViewDimension] Dimension007
  AngleOverride = false
  Arbitrary = false
  ArbitraryTolerances = false
  EqualTolerance = true
  ExtensionAngle = 0
  FormatSpec = %.2w (1/8")
  FormatSpecOverTolerance = %+.2w
  FormatSpecUnderTolerance = %+.2w
  Inverted = false
  LineAngle = 0
  LockPosition = false
  MeasureType = 1
  OverTolerance = 0
  References2D = -> [View]
  Rotation = 0
  Scale = 0.5
  ScaleType = 0
  TheoreticalExact = false
  Type = 2
  UnderTolerance = 0
  X = -36.0526
  Y = 20.6653
FEATURE [TechDraw::DrawPage] Page
  KeepUpdated = true
  NextBalloonIndex = 1
  ProjectionType = 0
  Scale = 0.5
  Template = -> Template
  Views = -> [View001,View,Dimension001,Dimension,View002,Dimension004,Dimension005,Dimension006,Dimension007,Dimension008]
---- part Disk.FCStd = doc fcstd_f89027e864b7 ----
FCSTD DOCUMENT  (FreeCAD 0.21R33771 (Git))
Label: Disk
License: All rights reserved
LicenseURL: http://en.wikipedia.org/wiki/All_rights_reserved
objects: Sketcher::SketchObject×1, PartDesign::Pad×1, PartDesign::CoordinateSystem×1, PartDesign::Body×1
note: 5 computed .brp shape members not serialized (recipe doc carries the construction recipe); baked Part::Feature solids carry a one-line shape summary decoded from their .brp

FEATURE [Sketcher::SketchObject] Sketch010
  FullyConstrained = true
  MapMode = 5
  Support = -> [XY_Plane008]
  sketch-geometry (2):
    g0: Circle CenterX=0 CenterY=0 CenterZ=0 NormalX=0 NormalY=0 NormalZ=1 AngleXU=0 Radius=4
    g1: Circle CenterX=0 CenterY=0 CenterZ=0 NormalX=0 NormalY=0 NormalZ=1 AngleXU=0 Radius=60
  constraints (4):
    c: Coincident(g0,g-1)
    c: Coincident(g1,g0)
    c: Diameter(g0) = 8
    c: Diameter(g1) = 120
FEATURE [PartDesign::Pad] Pad003
  Direction = (0,0,1)
  Length = 9.525
  Length2 = 10
  Profile = -> Sketch010
  ReferenceAxis = -> Sketch010 [N_Axis]
  Type = 0
FEATURE [PartDesign::CoordinateSystem] Local_CS
  AttacherType = Attacher::AttachEngine3D
  MapMode = 11
  Placement = pos=(0,0,9.525) rot=(0,0,1;1.5708rad)
  Support = -> [Pad003]
FEATURE [PartDesign::Body] Body002  label="Disk"
  Group = -> [Sketch010,Pad003,Local_CS]
  Origin = -> Origin008
  Placement = pos=(45.0712,-32.9487,17.4918) rot=(0,0,1;0rad)
  Tip = -> Pad003
---- part Holder.FCStd = doc fcstd_1cdae65e5386 ----
FCSTD DOCUMENT  (FreeCAD 0.21R33771 (Git))
Label: Holder
License: All rights reserved
LicenseURL: http://en.wikipedia.org/wiki/All_rights_reserved
objects: TechDraw::DrawViewDimension×12, Sketcher::SketchObject×4, TechDraw::DrawProjGroupItem×4, PartDesign::Hole×2, PartDesign::CoordinateSystem×2, PartDesign::Revolution×1, TechDraw::DrawSVGTemplate×1, TechDraw::DrawProjGroup×1, TechDraw::DrawViewSection×1, PartDesign::Pocket×1, PartDesign::Mirrored×1, PartDesign::Body×1, TechDraw::DrawViewPart×1, TechDraw::DrawPage×1
note: 16 computed .brp shape members not serialized (recipe doc carries the construction recipe); baked Part::Feature solids carry a one-line shape summary decoded from their .brp

FEATURE [Sketcher::SketchObject] Sketch  label="cone"
  FullyConstrained = true
  MapMode = 5
  Placement = pos=(0,0,0) rot=(0.57735,0.57735,0.57735;2.0944rad)
  Support = -> [YZ_Plane]
  sketch-geometry (8):
    g0: LineSegment StartX=0 StartY=0 StartZ=0 EndX=0 EndY=35 EndZ=0
    g1: LineSegment StartX=0 StartY=35 StartZ=0 EndX=-30 EndY=35 EndZ=0
    g2: LineSegment StartX=-30 StartY=0 StartZ=0 EndX=0 EndY=0 EndZ=0
    g3: LineSegment StartX=-30 StartY=35 StartZ=0 EndX=-30 EndY=20 EndZ=0
    g4: LineSegment StartX=-30 StartY=20 StartZ=0 EndX=-25 EndY=15 EndZ=0
    g5: LineSegment StartX=-25 StartY=15 StartZ=0 EndX=-25 EndY=10 EndZ=0
    g6: LineSegment StartX=-25 StartY=10 StartZ=0 EndX=-30 EndY=5 EndZ=0
    g7: LineSegment StartX=-30 StartY=5 StartZ=0 EndX=-30 EndY=0 EndZ=0
  constraints (23):
    c: PointOnObject(g0,g-2)
    c: Coincident(g0,g1)
    c: Horizontal(g1)
    c: DistanceY(g-1,g0) = 35  'height'
    c: Coincident(g0,g-1)
    c: Coincident(g2,g0)
    c: Horizontal(g2)
    c: DistanceX(g1,g1) = 30  'width'
    c: Coincident(g1,g3)
    c: Vertical(g3)
    c: Coincident(g3,g4)
    c: Coincident(g4,g5)
    c: Vertical(g5)
    c: Coincident(g5,g6)
    c: Coincident(g6,g7)
    c: Coincident(g7,g2)
    c: Vertical(g7)
    c: Angle(g7,g6) = 2.35619
    c: Angle(g4,g3) = 2.35619
    c: Vertical(g6,g3)
    c: DistanceY(g7,g7) = 5
    c: DistanceY(g5,g5) = 5
    c: DistanceY(g3,g3) = 15
FEATURE [PartDesign::Revolution] Revolution  label="Cone"
  Angle = 360
  Axis = (-2e-16,3e-16,1)
  Base = (0,0,0)
  Profile = -> Sketch
  ReferenceAxis = -> Sketch [V_Axis]
FEATURE [Sketcher::SketchObject] Sketch001  label="slot"
  FullyConstrained = true
  MapMode = 5
  Placement = pos=(0,0,0) rot=(0.57735,0.57735,0.57735;2.0944rad)
  Support = -> [YZ_Plane]
  expr: Constraints[10] = <<cone>>.Constraints.height
  sketch-geometry (4):
    g0: LineSegment StartX=14.5 StartY=35 StartZ=0 EndX=14.5 EndY=20.5 EndZ=0
    g1: LineSegment StartX=14.5 StartY=20.5 StartZ=0 EndX=-14.5 EndY=20.5 EndZ=0
    g2: LineSegment StartX=-14.5 StartY=20.5 StartZ=0 EndX=-14.5 EndY=35 EndZ=0
    g3: LineSegment StartX=-14.5 StartY=35 StartZ=0 EndX=14.5 EndY=35 EndZ=0
  constraints (11):
    c: Vertical(g0)
    c: Coincident(g0,g1)
    c: Horizontal(g1)
    c: Coincident(g1,g2)
    c: Vertical(g2)
    c: Symmetric(g2,g0,g-2)
    c: DistanceX(g1,g1) = 29  'width'
    c: Coincident(g3,g2)
    c: Coincident(g3,g0)
    c: DistanceY(g0,g0) = 14.5
    c: DistanceY(g-1,g0) = 35
FEATURE [Sketcher::SketchObject] Sketch002  label="hole"
  AttachmentOffset = pos=(0,0,30) rot=(0,0,1;0rad)
  FullyConstrained = true
  MapMode = 5
  Placement = pos=(0,-30,-6.7e-15) rot=(1,0,0;1.5708rad)
  Support = -> [XZ_Plane]
  expr: .AttachmentOffset.Base.z = Sketch.Constraints.width
  expr: Constraints[1] = <<cone>>.Constraints.height - 5 mm
  sketch-geometry (2):
    g0: Circle CenterX=-12.5 CenterY=30 CenterZ=0 NormalX=0 NormalY=0 NormalZ=1 AngleXU=0 Radius=1.25
    g1: Circle CenterX=12.5 CenterY=30 CenterZ=0 NormalX=0 NormalY=0 NormalZ=1 AngleXU=0 Radius=1.25
  constraints (5):
    c: Diameter(g0) = 2.5
    c: DistanceY(g-1,g0) = 30
    c: Equal(g1,g0)
    c: Symmetric(g1,g0,g-2)
    c: DistanceX(g0,g1) = 25
FEATURE [Sketcher::SketchObject] Sketch003  label="thread"
  FullyConstrained = true
  MapMode = 5
  Support = -> [XY_Plane]
  sketch-geometry (1):
    g0: Circle CenterX=0 CenterY=0 CenterZ=0 NormalX=0 NormalY=0 NormalZ=1 AngleXU=0 Radius=3.5
  constraints (2):
    c: Coincident(g0,g-1)
    c: Diameter(g0) = 7
FEATURE [TechDraw::DrawSVGTemplate] Template
  Height = 297
  Orientation = 1
  Width = 420
FEATURE [TechDraw::DrawProjGroupItem] ProjItem  label="Front"
  CoarseView = false
  Direction = (-1,0,0)
  Focus = 100
  HardHidden = false
  IsoCount = 0
  IsoHidden = false
  IsoVisible = false
  LockPosition = true
  Perspective = false
  Rotation = 0
  RotationVector = (0,-1,0)
  ScaleType = 2
  ScrubCount = 0
  SeamHidden = false
  SeamVisible = true
  SmoothHidden = false
  SmoothVisible = true
  Type = 0
  X = 0
  XDirection = (0,-1,0)
  Y = 0
FEATURE [TechDraw::DrawProjGroupItem] ProjItem003  label="Top"
  CoarseView = false
  Direction = (0,0,1)
  Focus = 100
  HardHidden = true
  IsoCount = 0
  IsoHidden = false
  IsoVisible = false
  LockPosition = false
  Perspective = false
  Rotation = 0
  RotationVector = (1,0,0)
  ScaleType = 2
  ScrubCount = 0
  SeamHidden = false
  SeamVisible = true
  SmoothHidden = false
  SmoothVisible = true
  Type = 4
  X = 0
  XDirection = (0,-1,0)
  Y = 85.7124
FEATURE [TechDraw::DrawProjGroupItem] ProjItem002  label="Bottom"
  CoarseView = false
  Direction = (0,0,-1)
  Focus = 100
  HardHidden = false
  IsoCount = 0
  IsoHidden = false
  IsoVisible = false
  LockPosition = false
  Perspective = false
  Rotation = 0
  RotationVector = (1,0,0)
  ScaleType = 2
  ScrubCount = 0
  SeamHidden = false
  SeamVisible = true
  SmoothHidden = false
  SmoothVisible = true
  Type = 5
  X = 0
  XDirection = (0,-1,0)
  Y = -79.9093
FEATURE [TechDraw::DrawViewDimension] Dimension004
  AngleOverride = false
  Arbitrary = true
  ArbitraryTolerances = false
  EqualTolerance = true
  ExtensionAngle = 0
  FormatSpec = M8 ↧15
  FormatSpecOverTolerance = %+.2w
  FormatSpecUnderTolerance = %+.2w
  Inverted = false
  LineAngle = 0
  LockPosition = false
  MeasureType = 1
  OverTolerance = 0
  References2D = -> [ProjItem002]
  Rotation = 0
  ScaleType = 0
  TheoreticalExact = false
  Type = 5
  UnderTolerance = 0
  X = -63.7982
  Y = 30.8498
FEATURE [TechDraw::DrawViewDimension] Dimension
  AngleOverride = false
  Arbitrary = false
  ArbitraryTolerances = false
  EqualTolerance = true
  ExtensionAngle = 0
  FormatSpec = ⌀%.2w
  FormatSpecOverTolerance = %+.2w
  FormatSpecUnderTolerance = %+.2w
  Inverted = false
  LineAngle = 0
  LockPosition = false
  MeasureType = 1
  OverTolerance = 0
  References2D = -> [ProjItem002]
  Rotation = 0
  ScaleType = 0
  TheoreticalExact = false
  Type = 5
  UnderTolerance = 0
  X = -70.3298
  Y = -13.9289
FEATURE [TechDraw::DrawProjGroupItem] ProjItem004  label="Right"
  CoarseView = false
  Direction = (-1e-16,-1,0)
  Focus = 100
  HardHidden = false
  IsoCount = 0
  IsoHidden = false
  IsoVisible = true
  LockPosition = false
  Perspective = false
  Rotation = 0
  RotationVector = (1,0,0)
  ScaleType = 2
  ScrubCount = 0
  SeamHidden = false
  SeamVisible = false
  SmoothHidden = false
  SmoothVisible = true
  Type = 2
  X = 110.789
  XDirection = (1,-1e-16,0)
  Y = 0
FEATURE [TechDraw::DrawProjGroup] ProjGroup
  Anchor = -> ProjItem
  AutoDistribute = false
  LockPosition = false
  ProjectionType = 1
  Rotation = 0
  ScaleType = 0
  Views = -> [ProjItem,ProjItem002,ProjItem003,ProjItem004]
  X = 124.891
  Y = 143.381
  spacingX = 15
  spacingY = 15
FEATURE [TechDraw::DrawViewDimension] Dimension011
  AngleOverride = false
  Arbitrary = false
  ArbitraryTolerances = false
  EqualTolerance = true
  ExtensionAngle = 0
  FormatSpec = %.2w
  FormatSpecOverTolerance = %+.2w
  FormatSpecUnderTolerance = %+.2w
  Inverted = false
  LineAngle = 0
  LockPosition = false
  MeasureType = 1
  OverTolerance = 0
  References2D = -> [ProjItem004]
  Rotation = 0
  ScaleType = 0
  TheoreticalExact = false
  Type = 1
  UnderTolerance = 0
  X = -28.2589
  Y = 35.4152
FEATURE [TechDraw::DrawViewDimension] Dimension009
  AngleOverride = false
  Arbitrary = false
  ArbitraryTolerances = false
  EqualTolerance = true
  ExtensionAngle = 0
  FormatSpec = 4X ⌀%.2w THRU ⌴⌀6↧4.5
  FormatSpecOverTolerance = %+.2w
  FormatSpecUnderTolerance = %+.2w
  Inverted = false
  LineAngle = 0
  LockPosition = false
  MeasureType = 1
  OverTolerance = 0
  References2D = -> [ProjItem004]
  Rotation = 0
  ScaleType = 0
  TheoreticalExact = false
  Type = 5
  UnderTolerance = 0
  X = 72.9187
  Y = -1.0129
FEATURE [TechDraw::DrawViewSection] SectionView  label="Section A - A"
  BaseView = -> ProjItem003
  CoarseView = false
  CutSurfaceDisplay = 2
  Direction = (-1,-1e-16,0)
  FileGeomPattern = <path>
  FileHatchPattern = <path>
  Focus = 100
  FuseBeforeCut = false
  HardHidden = false
  HatchOffset = (0,0,0)
  HatchRotation = 0
  HatchScale = 1
  IsoCount = 0
  IsoHidden = false
  IsoVisible = true
  LockPosition = false
  NameGeomPattern = Diamond
  Perspective = false
  Rotation = 0
  ScaleType = 2
  ScrubCount = 0
  SeamHidden = false
  SeamVisible = true
  SectionDirection = 0
  SectionNormal = (-1,-1e-16,0)
  SectionOrigin = (0,0,17.51)
  SectionSymbol = A
  SmoothHidden = false
  SmoothVisible = true
  TrimAfterCut = false
  X = 236.253
  XDirection = (1e-16,-1,0)
  Y = 220.836
FEATURE [TechDraw::DrawViewDimension] Dimension007
  AngleOverride = false
  Arbitrary = false
  ArbitraryTolerances = false
  EqualTolerance = true
  ExtensionAngle = 0
  FormatSpec = %.2w
  FormatSpecOverTolerance = %+.2w
  FormatSpecUnderTolerance = %+.2w
  Inverted = false
  LineAngle = 0
  LockPosition = false
  MeasureType = 1
  OverTolerance = 0
  References2D = -> [SectionView]
  Rotation = 0
  ScaleType = 0
  TheoreticalExact = false
  Type = 6
  UnderTolerance = 0
  X = 47.7226
  Y = -6.41254
FEATURE [TechDraw::DrawViewDimension] Dimension010
  AngleOverride = false
  Arbitrary = false
  ArbitraryTolerances = false
  EqualTolerance = true
  ExtensionAngle = 0
  FormatSpec = %.2w
  FormatSpecOverTolerance = %+.2w
  FormatSpecUnderTolerance = %+.2w
  Inverted = false
  LineAngle = 0
  LockPosition = false
  MeasureType = 1
  OverTolerance = 0
  References2D = -> [SectionView]
  Rotation = 0
  ScaleType = 0
  TheoreticalExact = false
  Type = 1
  UnderTolerance = 0
  X = 0.247712
  Y = 49.9322
FEATURE [TechDraw::DrawViewDimension] Dimension006
  AngleOverride = false
  Arbitrary = false
  ArbitraryTolerances = false
  EqualTolerance = true
  ExtensionAngle = 0
  FormatSpec = %.2w
  FormatSpecOverTolerance = %+.2w
  FormatSpecUnderTolerance = %+.2w
  Inverted = false
  LineAngle = 0
  LockPosition = false
  MeasureType = 1
  OverTolerance = 0
  References2D = -> [Dimension007,SectionView]
  Rotation = 0
  ScaleType = 0
  TheoreticalExact = false
  Type = 2
  UnderTolerance = 0
  X = -49.0556
  Y = 34.2523
FEATURE [TechDraw::DrawViewDimension] Dimension005
  AngleOverride = false
  Arbitrary = false
  ArbitraryTolerances = false
  EqualTolerance = true
  ExtensionAngle = 0
  FormatSpec = %.2w
  FormatSpecOverTolerance = %+.2w
  FormatSpecUnderTolerance = %+.2w
  Inverted = false
  LineAngle = 0
  LockPosition = false
  MeasureType = 1
  OverTolerance = 0
  References2D = -> [SectionView]
  Rotation = 0
  ScaleType = 0
  TheoreticalExact = false
  Type = 1
  UnderTolerance = 0
  X = 0.190286
  Y = 36.7069
FEATURE [TechDraw::DrawViewDimension] Dimension013
  AngleOverride = false
  Arbitrary = false
  ArbitraryTolerances = false
  EqualTolerance = true
  ExtensionAngle = 0
  FormatSpec = %.2w
  FormatSpecOverTolerance = %+.2w
  FormatSpecUnderTolerance = %+.2w
  Inverted = false
  LineAngle = 0
  LockPosition = false
  MeasureType = 1
  OverTolerance = 0
  References2D = -> [ProjItem]
  Rotation = 0
  ScaleType = 0
  TheoreticalExact = false
  Type = 2
  UnderTolerance = 0
  X = -66.3225
  Y = 1.97021
FEATURE [TechDraw::DrawViewDimension] Dimension014
  AngleOverride = false
  Arbitrary = false
  ArbitraryTolerances = false
  EqualTolerance = true
  ExtensionAngle = 0
  FormatSpec = %.2w
  FormatSpecOverTolerance = %+.2w
  FormatSpecUnderTolerance = %+.2w
  Inverted = false
  LineAngle = 0
  LockPosition = false
  MeasureType = 1
  OverTolerance = 0
  References2D = -> [ProjItem004]
  Rotation = 0
  ScaleType = 0
  TheoreticalExact = false
  Type = 2
  UnderTolerance = 0
  X = -46.9361
  Y = -1.01148
FEATURE [TechDraw::DrawViewDimension] Dimension015
  AngleOverride = false
  Arbitrary = false
  ArbitraryTolerances = false
  EqualTolerance = true
  ExtensionAngle = 0
  FormatSpec = %.2w
  FormatSpecOverTolerance = %+.2w
  FormatSpecUnderTolerance = %+.2w
  Inverted = false
  LineAngle = 0
  LockPosition = false
  MeasureType = 1
  OverTolerance = 0
  References2D = -> [ProjItem]
  Rotation = 0
  ScaleType = 0
  TheoreticalExact = false
  Type = 2
  UnderTolerance = 0
  X = -42.7174
  Y = -28.1212
FEATURE [TechDraw::DrawViewDimension] Dimension016
  AngleOverride = false
  Arbitrary = false
  ArbitraryTolerances = false
  EqualTolerance = true
  ExtensionAngle = 0
  FormatSpec = %.2w
  FormatSpecOverTolerance = %+.2w
  FormatSpecUnderTolerance = %+.2w
  Inverted = false
  LineAngle = 0
  LockPosition = false
  MeasureType = 1
  OverTolerance = 0
  References2D = -> [ProjItem]
  Rotation = 0
  ScaleType = 0
  TheoreticalExact = false
  Type = 2
  UnderTolerance = 0
  X = -52.9399
  Y = -28.141
FEATURE [PartDesign::Pocket] Pocket
  BaseFeature = -> Revolution
  Direction = (-1,2e-16,-3e-16)
  Length = 5
  Length2 = 5
  Midplane = true
  Profile = -> Sketch001
  ReferenceAxis = -> Sketch001 [N_Axis]
  Type = 1
FEATURE [PartDesign::Hole] Hole
  BaseFeature = -> Pocket
  CustomThreadClearance = 0
  Depth = 30
  DepthType = 0
  Diameter = 2.5
  DrillForDepth = false
  DrillPoint = 1
  DrillPointAngle = 118
  HoleCutCountersinkAngle = 90
  HoleCutCustomValues = false
  HoleCutDepth = 4.5
  HoleCutDiameter = 6
  HoleCutType = 1
  ModelThread = false
  Profile = -> Sketch002 [Edge1,Edge2]
  Tapered = false
  TaperedAngle = 90
  ThreadClass = 0
  ThreadDepth = 30
  ThreadDepthType = 0
  ThreadDirection = 0
  ThreadFit = 0
  ThreadSize = 9
  ThreadType = 1
  Threaded = true
  UseCustomThreadClearance = false
  expr: Depth = Sketch.Constraints.width
FEATURE [PartDesign::Mirrored] Mirrored
  BaseFeature = -> Hole
  MirrorPlane = -> XZ_Plane
  Originals = -> [Hole]
FEATURE [PartDesign::Hole] Hole001
  BaseFeature = -> Mirrored
  CustomThreadClearance = 0
  Depth = 15
  DepthType = 0
  Diameter = 9
  DrillForDepth = false
  DrillPoint = 1
  DrillPointAngle = 118
  HoleCutCountersinkAngle = 90
  HoleCutCustomValues = false
  HoleCutDepth = 0
  HoleCutDiameter = 6.1
  HoleCutType = 0
  ModelThread = false
  Profile = -> Sketch003
  Reversed = true
  Tapered = false
  TaperedAngle = 90
  ThreadClass = 0
  ThreadDepth = 15
  ThreadDepthType = 0
  ThreadDirection = 0
  ThreadFit = 0
  ThreadSize = 16
  ThreadType = 1
  Threaded = false
  UseCustomThreadClearance = false
FEATURE [PartDesign::CoordinateSystem] Local_CS
  AttacherType = Attacher::AttachEngine3D
  MapMode = 11
  Placement = pos=(0,0,0) rot=(0.707107,0.707107,0;3.14159rad)
  Support = -> [Hole001]
FEATURE [PartDesign::CoordinateSystem] Local_CS001
  AttacherType = Attacher::AttachEngine3D
  MapMode = 45
  Placement = pos=(1.3e-15,4.8e-15,20.5) rot=(0,0,1;1.5708rad)
  Support = -> [Hole001]
FEATURE [PartDesign::Body] Body  label="Holder"
  Group = -> [Sketch,Revolution,Sketch001,Sketch002,Pocket,Hole,Sketch003,Mirrored,Local_CS,Local_CS001,Hole001]
  Origin = -> Origin
  Tip = -> Hole001
FEATURE [TechDraw::DrawViewPart] View  label="Iso"
  CoarseView = false
  Direction = (-0.577,-0.577,0.577)
  Focus = 100
  HardHidden = false
  IsoCount = 0
  IsoHidden = false
  IsoVisible = false
  LockPosition = false
  Perspective = false
  Rotation = 0
  ScaleType = 0
  ScrubCount = 0
  SeamHidden = false
  SeamVisible = false
  SmoothHidden = false
  SmoothVisible = true
  Source = -> [Body]
  X = 350.974
  XDirection = (0.707,-0.707,0)
  Y = 218.276
FEATURE [TechDraw::DrawPage] Page
  KeepUpdated = true
  NextBalloonIndex = 1
  ProjectionType = 0
  Template = -> Template
  Views = -> [ProjGroup,View,Dimension004,SectionView,Dimension,Dimension005,Dimension006,Dimension007,Dimension009,Dimension010,Dimension011,Dimension013,Dimension014,Dimension015,Dimension016]
note: 2 file-system paths scrubbed to <path> (originals preserved in the JSON sidecar)
---- part Pin.FCStd = doc fcstd_60ada35b86dc ----
FCSTD DOCUMENT  (FreeCAD 0.21R33771 (Git))
Label: Pin
License: All rights reserved
LicenseURL: http://en.wikipedia.org/wiki/All_rights_reserved
objects: Sketcher::SketchObject×2, PartDesign::Pad×1, PartDesign::Hole×1, PartDesign::CoordinateSystem×1, PartDesign::Body×1
note: 8 computed .brp shape members not serialized (recipe doc carries the construction recipe); baked Part::Feature solids carry a one-line shape summary decoded from their .brp

FEATURE [Sketcher::SketchObject] Sketch
  FullyConstrained = true
  MapMode = 5
  Placement = pos=(0,0,0) rot=(1,0,0;1.5708rad)
  Support = -> [XZ_Plane]
  sketch-geometry (1):
    g0: Circle CenterX=0 CenterY=0 CenterZ=0 NormalX=0 NormalY=0 NormalZ=1 AngleXU=0 Radius=6
  constraints (2):
    c: Coincident(g0,g-1)
    c: Diameter(g0) = 12
FEATURE [PartDesign::Pad] Pad
  Direction = (0,-1,-2e-16)
  Length = 38.1
  Length2 = 10
  Midplane = true
  Placement = pos=(0,0,0) rot=(1,0,0;1.5708rad)
  Profile = -> Sketch
  ReferenceAxis = -> Sketch [N_Axis]
  Type = 0
FEATURE [Sketcher::SketchObject] Sketch001
  AttachmentOffset = pos=(0,0,17) rot=(0,0,1;0rad)
  FullyConstrained = true
  MapMode = 5
  Placement = pos=(17,-3.8e-15,3.8e-15) rot=(0.57735,0.57735,0.57735;2.0944rad)
  Support = -> [YZ_Plane]
  sketch-geometry (1):
    g0: Circle CenterX=0 CenterY=0 CenterZ=0 NormalX=0 NormalY=0 NormalZ=1 AngleXU=0 Radius=4
  constraints (2):
    c: Coincident(g0,g-1)
    c: Diameter(g0) = 8
FEATURE [PartDesign::Hole] Hole
  BaseFeature = -> Pad
  CustomThreadClearance = 0
  Depth = 115.185
  DepthType = 1
  Diameter = 6.8
  DrillForDepth = false
  DrillPoint = 1
  DrillPointAngle = 118
  HoleCutCountersinkAngle = 90
  HoleCutCustomValues = false
  HoleCutDepth = 0
  HoleCutDiameter = 0
  HoleCutType = 0
  ModelThread = false
  Placement = pos=(0,0,0) rot=(1,0,0;1.5708rad)
  Profile = -> Sketch001
  Tapered = false
  TaperedAngle = 90
  ThreadClass = 0
  ThreadDepth = 115.185
  ThreadDepthType = 0
  ThreadDirection = 0
  ThreadFit = 0
  ThreadSize = 16
  ThreadType = 1
  Threaded = true
  UseCustomThreadClearance = false
FEATURE [PartDesign::CoordinateSystem] Local_CS
  AttacherType = Attacher::AttachEngine3D
  Support = -> [Origin]
FEATURE [PartDesign::Body] Body  label="Pin"
  Group = -> [Sketch,Pad,Sketch001,Hole,Local_CS]
  Origin = -> Origin
  Tip = -> Hole
---- part Spacer.FCStd = doc fcstd_263d8eeaf14d ----
FCSTD DOCUMENT  (FreeCAD 0.21R33771 (Git))
Label: Spacer
License: All rights reserved
LicenseURL: http://en.wikipedia.org/wiki/All_rights_reserved
objects: Sketcher::SketchObject×2, PartDesign::CoordinateSystem×2, PartDesign::Revolution×1, PartDesign::Pocket×1, PartDesign::Body×1
note: 9 computed .brp shape members not serialized (recipe doc carries the construction recipe); baked Part::Feature solids carry a one-line shape summary decoded from their .brp

FEATURE [Sketcher::SketchObject] Sketch
  FullyConstrained = true
  MapMode = 5
  Placement = pos=(0,0,0) rot=(1,0,0;1.5708rad)
  Support = -> [XZ_Plane]
  sketch-geometry (5):
    g0: LineSegment StartX=0 StartY=0 StartZ=0 EndX=0 EndY=11 EndZ=0
    g1: LineSegment StartX=0 StartY=11 StartZ=0 EndX=7.5 EndY=11 EndZ=0
    g2: LineSegment StartX=7.5 StartY=11 StartZ=0 EndX=16 EndY=8 EndZ=0
    g3: LineSegment StartX=16 StartY=8 StartZ=0 EndX=16 EndY=0 EndZ=0
    g4: LineSegment StartX=16 StartY=0 StartZ=0 EndX=0 EndY=0 EndZ=0
  constraints (14):
    c: Coincident(g0,g-1)
    c: PointOnObject(g0,g-2)
    c: Horizontal(g1)
    c: Coincident(g3,g2)
    c: Vertical(g3)
    c: Coincident(g4,g0)
    c: Horizontal(g4)
    c: DistanceY(g3,g3) = 8
    c: DistanceY(g0,g0) = 11
    c: DistanceX(g4,g4) = 16
    c: DistanceX(g1,g1) = 7.5
    c: Coincident(g1,g0)
    c: Coincident(g1,g2)
    c: Coincident(g3,g4)
FEATURE [PartDesign::Revolution] Revolution
  Angle = 360
  Axis = (0,-2e-16,1)
  Base = (0,0,0)
  Placement = pos=(0,0,0) rot=(1,0,0;1.5708rad)
  Profile = -> Sketch
  ReferenceAxis = -> Sketch [V_Axis]
  Reversed = true
FEATURE [Sketcher::SketchObject] Sketch001
  FullyConstrained = true
  MapMode = 5
  Support = -> [XY_Plane]
  sketch-geometry (1):
    g0: Circle CenterX=0 CenterY=0 CenterZ=0 NormalX=0 NormalY=0 NormalZ=1 AngleXU=0 Radius=4
  constraints (2):
    c: Coincident(g0,g-1)
    c: Diameter(g0) = 8
FEATURE [PartDesign::Pocket] Pocket
  BaseFeature = -> Revolution
  Direction = (0,0,-1)
  Length = 5
  Length2 = 5
  Placement = pos=(0,0,0) rot=(1,0,0;1.5708rad)
  Profile = -> Sketch001
  ReferenceAxis = -> Sketch001 [N_Axis]
  Reversed = true
  Type = 1
FEATURE [PartDesign::CoordinateSystem] Local_CS
  AttacherType = Attacher::AttachEngine3D
  MapMode = 11
  Placement = pos=(0,4.9e-15,11) rot=(0.707107,-0.707107,0;3.14159rad)
  Support = -> [Pocket]
FEATURE [PartDesign::CoordinateSystem] Local_CS001
  AttacherType = Attacher::AttachEngine3D
  MapMode = 11
  Placement = pos=(0,0,0) rot=(0,0,1;1.5708rad)
  Support = -> [Pocket]
FEATURE [PartDesign::Body] Body  label="Spacer"
  Group = -> [Sketch,Revolution,Sketch001,Pocket,Local_CS,Local_CS001]
  Origin = -> Origin
  Tip = -> Pocket
